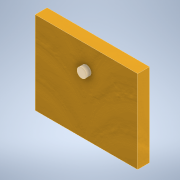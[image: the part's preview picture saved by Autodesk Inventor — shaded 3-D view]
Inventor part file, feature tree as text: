
AUTODESK INVENTOR PART (.ipt)
format: ipt  version: 2022.2 (Build 262287010, 287A)  size: 120,320 bytes
history: native  units: in
note: dims shown in document units (in); Inventor stores cm internally (conversion verified against a paired STEP export)
features: extrude x2, sketch x2, other x1
ambient origin geometry x8: Origin, YZ Plane, XZ Plane, XY Plane, X Axis, Y Axis, Z Axis, Center Point
bodies: Body1 (feature_tree)
feature tree (5):
  other  "Sólido1"
  extrude  "Extrusión1"  Depth=1.378in
  extrude  "Extrusión2"  Depth=0.1969in TaperAngle=0.0deg
  sketch  "Boceto1"  dims[d0=1.6986in d1=1.378in]
  sketch  "Boceto3"  dims[d3=0.1378in d4=0.1969in d5=0.0in d6=0.1575in d7=0.0787in d8=0.0in]
